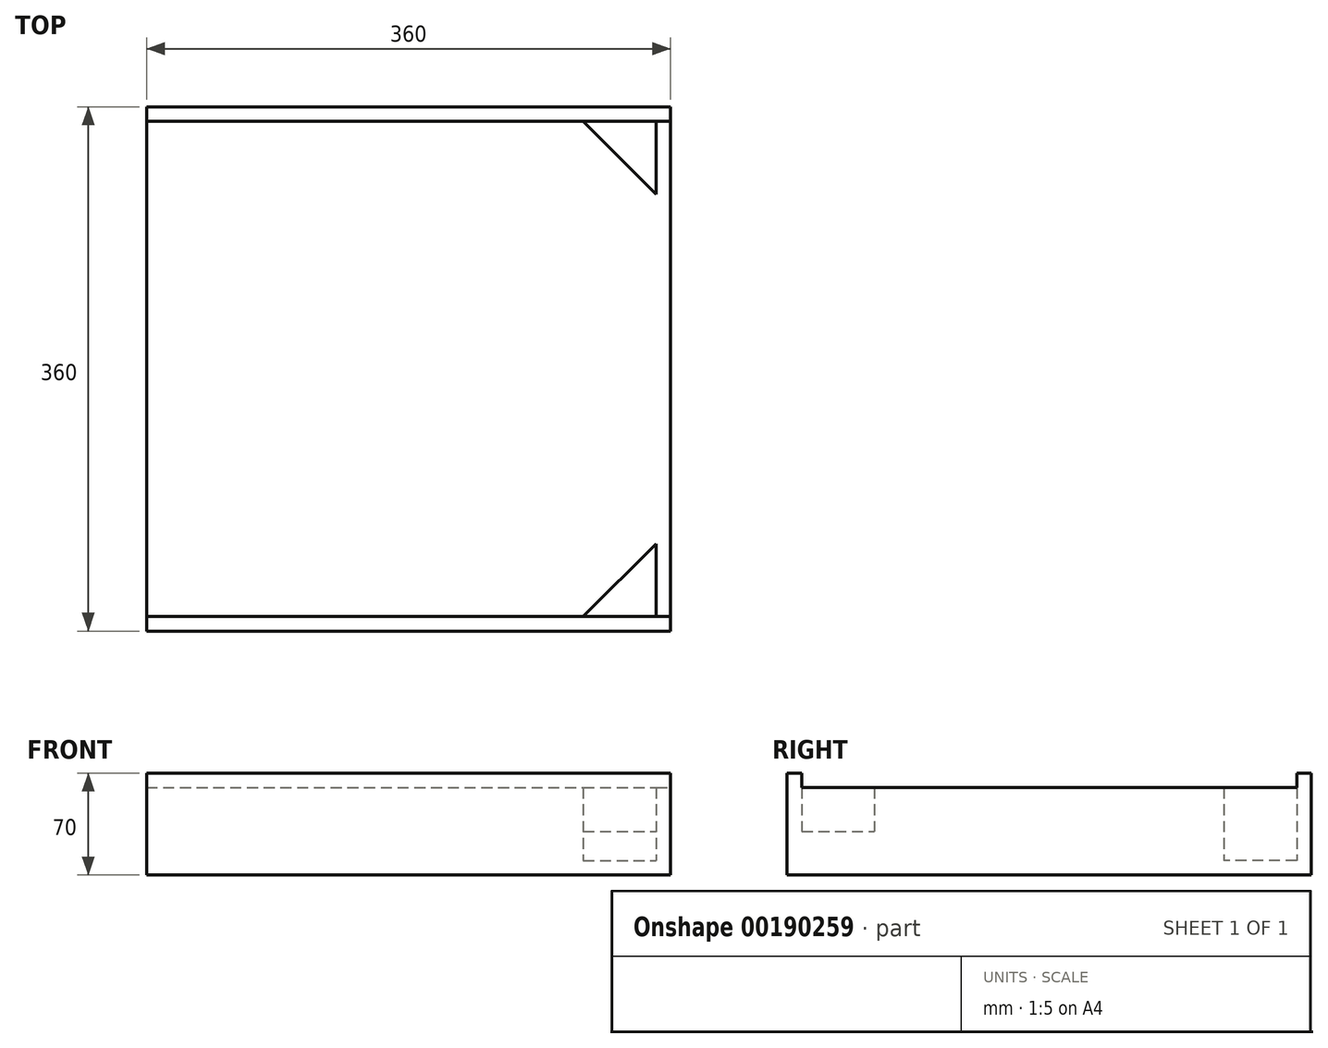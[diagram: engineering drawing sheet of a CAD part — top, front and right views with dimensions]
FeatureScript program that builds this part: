
annotation { "Feature Type Name" : "Feature", "Feature Type Description" : "" }
export const myFeature = defineFeature(function(context is Context, id is Id, definition is map)
    precondition{}
    {
        {
            assignVariable(context, id + "F0", {"name" : "Epb1", "anyValue" : 10});
        }
        {
            var Q0;
            Q0=qCreatedBy(makeId("Top.planeOp"),FACE);
            var sketch = newSketch(context, id + "F1", { "sketchPlane" : qUnion([Q0])});
            skCircle(sketch, "E0", {"center": v(0, 0) * mm, "radius": 150 * mm});
            skSolve(sketch);
        }
        {
            var Q0;
            Q0=makeQuery(id+"F1.imprint","IMPRINT",FACE,{"disambiguationData":[TD([[makeQuery(id+"F1.imprint","IMPRINT",EDGE,{"derivedFrom":sQuery(id+"F1.wireOp",EDGE,"E0")}),1.0]])]});
            extrude(context, id + "F2", {"entities" : qUnion([Q0]), "depth" : 35 * mm});
        }
        {
            var Q0;
            Q0=makeQuery(id+"F2.opExtrude","CAP_FACE",FACE,{"disambiguationData":[OSD([sQuery(id+"F1.wireOp",EDGE,"E0")])],"isStart":true});
            var sketch = newSketch(context, id + "F3", { "sketchPlane" : qUnion([Q0])});
            skLineSegment(sketch, "E1.bottom", {"start": v(-170, 170) * mm, "end": v(170, 170) * mm});
            skLineSegment(sketch, "E1.top", {"start": v(-170, -170) * mm, "end": v(170, -170) * mm});
            skLineSegment(sketch, "E1.left", {"start": v(-170, 170) * mm, "end": v(-170, -170) * mm});
            skLineSegment(sketch, "E1.right", {"start": v(170, 170) * mm, "end": v(170, -170) * mm});
            skPoint(sketch, "E1.middle", {"position": v(0, 0) * mm});
            skLineSegment(sketch, "E2", {"start": v(170, -170) * mm, "end": v(120, -170) * mm});
            skLineSegment(sketch, "E3", {"start": v(170, -170) * mm, "end": v(170, -120) * mm});
            skLineSegment(sketch, "E4", {"start": v(170, -120) * mm, "end": v(120, -170) * mm});
            skLineSegment(sketch, "E5.1.0", {"start": v(-170, -170) * mm, "end": v(-170, -120) * mm});
            skLineSegment(sketch, "E5.1.1", {"start": v(-170, -170) * mm, "end": v(-120, -170) * mm});
            skLineSegment(sketch, "E5.1.2", {"start": v(-120, -170) * mm, "end": v(-170, -120) * mm});
            skLineSegment(sketch, "E5.2.0", {"start": v(-170, 170) * mm, "end": v(-120, 170) * mm});
            skLineSegment(sketch, "E5.2.1", {"start": v(-170, 170) * mm, "end": v(-170, 120) * mm});
            skLineSegment(sketch, "E5.2.2", {"start": v(-170, 120) * mm, "end": v(-120, 170) * mm});
            skLineSegment(sketch, "E5.3.0", {"start": v(170, 170) * mm, "end": v(170, 120) * mm});
            skLineSegment(sketch, "E5.3.1", {"start": v(170, 170) * mm, "end": v(120, 170) * mm});
            skLineSegment(sketch, "E5.3.2", {"start": v(120, 170) * mm, "end": v(170, 120) * mm});
            skLineSegment(sketch, "E5.anchor1", {"start": v(0, 0) * mm, "end": v(120, -170) * mm, "construction": true});
            skLineSegment(sketch, "E5.anchor2", {"start": v(0, 0) * mm, "end": v(170, 120) * mm, "construction": true});
            skSolve(sketch);
        }
        {
            var Q0;
            Q0=makeQuery(id+"F3.imprint","IMPRINT",FACE,{"disambiguationData":[TD([[makeQuery(id+"F3.imprint","IMPRINT",EDGE,{"derivedFrom":sQuery(id+"F3.wireOp",EDGE,"E1.bottom")}),-1.0]])]});
            var Q1;
            Q1=makeQuery(id+"F3.imprint","IMPRINT",FACE,{"disambiguationData":[TD([[makeQuery(id+"F3.imprint","IMPRINT",EDGE,{"derivedFrom":makeQuery(id+"F2.opExtrude","CAP_EDGE",EDGE,{"disambiguationData":[OSD([sQuery(id+"F1.wireOp",EDGE,"E0")])],"isStart":true})}),-1.0]])]});
            extrude(context, id + "F4", {"entities" : qUnion([Q0, Q1]), "depth" : 10 * mm});
        }
        {
            var Q0;
            Q0=makeQuery(id+"F4.opExtrude","CAP_FACE",FACE,{"disambiguationData":[OSD([sQuery(id+"F3.wireOp",EDGE,"E1.bottom"),sQuery(id+"F3.wireOp",EDGE,"E1.top"),sQuery(id+"F3.wireOp",EDGE,"E1.left"),sQuery(id+"F3.wireOp",EDGE,"E1.right"),sQuery(id+"F3.wireOp",EDGE,"E4"),sQuery(id+"F3.wireOp",EDGE,"E5.1.2"),sQuery(id+"F3.wireOp",EDGE,"E5.2.2"),sQuery(id+"F3.wireOp",EDGE,"E5.3.2")])],"isStart":true});
            extrude(context, id + "F5", {"entities" : qUnion([Q0]), "depth" : 10 * mm});
        }
        {
            var Q0;
            Q0=makeQuery(id+"F4.opExtrude","CAP_FACE",FACE,{"disambiguationData":[OSD([sQuery(id+"F3.wireOp",EDGE,"E1.bottom"),sQuery(id+"F3.wireOp",EDGE,"E1.top"),sQuery(id+"F3.wireOp",EDGE,"E1.left"),sQuery(id+"F3.wireOp",EDGE,"E1.right"),sQuery(id+"F3.wireOp",EDGE,"E4"),sQuery(id+"F3.wireOp",EDGE,"E5.1.2"),sQuery(id+"F3.wireOp",EDGE,"E5.2.2"),sQuery(id+"F3.wireOp",EDGE,"E5.3.2")])],"isStart":false});
            var sketch = newSketch(context, id + "F6", { "sketchPlane" : qUnion([Q0])});
            skLineSegment(sketch, "E6.bottom", {"start": v(-180, 180) * mm, "end": v(180, 180) * mm});
            skLineSegment(sketch, "E6.top", {"start": v(-180, -180) * mm, "end": v(180, -180) * mm});
            skLineSegment(sketch, "E6.left", {"start": v(-180, 180) * mm, "end": v(-180, -180) * mm});
            skLineSegment(sketch, "E6.right", {"start": v(180, 180) * mm, "end": v(180, -180) * mm});
            skPoint(sketch, "E6.middle", {"position": v(0, 0) * mm});
            skSolve(sketch);
        }
        {
            var Q0;
            Q0=makeQuery(id+"F6.imprint","IMPRINT",FACE,{"disambiguationData":[TD([[makeQuery(id+"F6.imprint","IMPRINT",EDGE,{"derivedFrom":sQuery(id+"F6.wireOp",EDGE,"E6.bottom")}),-1.0]])]});
            var Q1;
            Q1=makeQuery(id+"F6.imprint","IMPRINT",FACE,{"disambiguationData":[TD([[makeQuery(id+"F6.imprint","IMPRINT",EDGE,{"derivedFrom":makeQuery(id+"F4.opExtrude","CAP_EDGE",EDGE,{"disambiguationData":[OSD([sQuery(id+"F3.wireOp",EDGE,"E1.bottom")])],"isStart":false})}),-1.0]])]});
            extrude(context, id + "F7", {"entities" : qUnion([Q0, Q1]), "depth" : (getVariable(context, 'Epb1')) * mm});
        }
        {
            var Q0;
            Q0=makeQuery(id+"F7.opExtrude","CAP_FACE",FACE,{"disambiguationData":[OSD([sQuery(id+"F6.wireOp",EDGE,"E6.bottom"),sQuery(id+"F6.wireOp",EDGE,"E6.top"),sQuery(id+"F6.wireOp",EDGE,"E6.left"),sQuery(id+"F6.wireOp",EDGE,"E6.right")])],"isStart":true});
            var sketch = newSketch(context, id + "F8", { "sketchPlane" : qUnion([Q0])});
            skLineSegment(sketch, "E7.bottom", {"start": v(-180, -180) * mm, "end": v(180, -180) * mm});
            skLineSegment(sketch, "E7.top", {"start": v(-180, -170) * mm, "end": v(180, -170) * mm});
            skLineSegment(sketch, "E7.left", {"start": v(-180, -180) * mm, "end": v(-180, -170) * mm});
            skLineSegment(sketch, "E7.right", {"start": v(180, -180) * mm, "end": v(180, -170) * mm});
            skLineSegment(sketch, "E8.bottom", {"start": v(-180, 180) * mm, "end": v(180, 180) * mm});
            skLineSegment(sketch, "E8.top", {"start": v(-180, 170) * mm, "end": v(180, 170) * mm});
            skLineSegment(sketch, "E8.left", {"start": v(-180, 180) * mm, "end": v(-180, 170) * mm});
            skLineSegment(sketch, "E8.right", {"start": v(180, 180) * mm, "end": v(180, 170) * mm});
            skLineSegment(sketch, "E9.bottom", {"start": v(-180, -170) * mm, "end": v(-170, -170) * mm});
            skLineSegment(sketch, "E9.top", {"start": v(-180, 170) * mm, "end": v(-170, 170) * mm});
            skLineSegment(sketch, "E9.left", {"start": v(-180, -170) * mm, "end": v(-180, 170) * mm});
            skLineSegment(sketch, "E9.right", {"start": v(-170, -170) * mm, "end": v(-170, 170) * mm});
            skLineSegment(sketch, "E10.bottom", {"start": v(180, -170) * mm, "end": v(170, -170) * mm});
            skLineSegment(sketch, "E10.top", {"start": v(180, 170) * mm, "end": v(170, 170) * mm});
            skLineSegment(sketch, "E10.left", {"start": v(180, -170) * mm, "end": v(180, 170) * mm});
            skLineSegment(sketch, "E10.right", {"start": v(170, -170) * mm, "end": v(170, 170) * mm});
            skSolve(sketch);
        }
        {
            var Q0;
            Q0=makeQuery(id+"F8.imprint","IMPRINT",FACE,{"disambiguationData":[TD([[makeQuery(id+"F8.imprint","IMPRINT",EDGE,{"derivedFrom":sQuery(id+"F8.wireOp",EDGE,"E7.bottom")}),1.0]])]});
            var Q1;
            Q1=makeQuery(id+"F8.imprint","IMPRINT",FACE,{"disambiguationData":[TD([[makeQuery(id+"F8.imprint","IMPRINT",EDGE,{"derivedFrom":sQuery(id+"F8.wireOp",EDGE,"E9.bottom")}),1.0]])]});
            var Q2;
            Q2=makeQuery(id+"F8.imprint","IMPRINT",FACE,{"disambiguationData":[TD([[makeQuery(id+"F8.imprint","IMPRINT",EDGE,{"derivedFrom":sQuery(id+"F8.wireOp",EDGE,"E8.bottom")}),-1.0]])]});
            var Q3;
            Q3=makeQuery(id+"F8.imprint","IMPRINT",FACE,{"disambiguationData":[TD([[makeQuery(id+"F8.imprint","IMPRINT",EDGE,{"derivedFrom":sQuery(id+"F8.wireOp",EDGE,"E10.bottom")}),-1.0]])]});
            extrude(context, id + "F9", {"entities" : qUnion([Q0, Q1, Q2, Q3]), "operationType" : NewBodyOperationType.ADD, "depth" : 60 * mm});
        }
        {
            var Q0;
            Q0=makeQuery(id+"F7.opExtrude","CAP_FACE",FACE,{"disambiguationData":[OSD([sQuery(id+"F6.wireOp",EDGE,"E6.bottom"),sQuery(id+"F6.wireOp",EDGE,"E6.top"),sQuery(id+"F6.wireOp",EDGE,"E6.left"),sQuery(id+"F6.wireOp",EDGE,"E6.right")])],"isStart":true});
            var sketch = newSketch(context, id + "F10", { "sketchPlane" : qUnion([Q0])});
            skLineSegment(sketch, "E11", {"start": v(170, -170) * mm, "end": v(120, -170) * mm});
            skLineSegment(sketch, "E12", {"start": v(170, -170) * mm, "end": v(170, -120) * mm});
            skLineSegment(sketch, "E13", {"start": v(170, -120) * mm, "end": v(120, -170) * mm});
            skLineSegment(sketch, "E14.1.0", {"start": v(170, 170) * mm, "end": v(170, 120) * mm});
            skLineSegment(sketch, "E14.1.1", {"start": v(120, 170) * mm, "end": v(170, 120) * mm});
            skLineSegment(sketch, "E14.1.2", {"start": v(170, 170) * mm, "end": v(120, 170) * mm});
            skLineSegment(sketch, "E14.2.0", {"start": v(-170, 170) * mm, "end": v(-120, 170) * mm});
            skLineSegment(sketch, "E14.2.1", {"start": v(-170, 120) * mm, "end": v(-120, 170) * mm});
            skLineSegment(sketch, "E14.2.2", {"start": v(-170, 170) * mm, "end": v(-170, 120) * mm});
            skLineSegment(sketch, "E14.3.0", {"start": v(-170, -170) * mm, "end": v(-170, -120) * mm});
            skLineSegment(sketch, "E14.3.1", {"start": v(-120, -170) * mm, "end": v(-170, -120) * mm});
            skLineSegment(sketch, "E14.3.2", {"start": v(-170, -170) * mm, "end": v(-120, -170) * mm});
            skPoint(sketch, "E14.center", {"position": v(0, 0) * mm});
            skSolve(sketch);
        }
        {
            var Q0;
            Q0=makeQuery(id+"F10.imprint","IMPRINT",FACE,{"disambiguationData":[TD([[makeQuery(id+"F10.imprint","IMPRINT",EDGE,{"derivedFrom":sQuery(id+"F10.wireOp",EDGE,"E14.3.0")}),-1.0]])]});
            var Q1;
            Q1=makeQuery(id+"F10.imprint","IMPRINT",FACE,{"disambiguationData":[TD([[makeQuery(id+"F10.imprint","IMPRINT",EDGE,{"derivedFrom":sQuery(id+"F10.wireOp",EDGE,"E11")}),1.0]])]});
            var Q2;
            Q2=makeQuery(id+"F10.imprint","IMPRINT",FACE,{"disambiguationData":[TD([[makeQuery(id+"F10.imprint","IMPRINT",EDGE,{"derivedFrom":sQuery(id+"F10.wireOp",EDGE,"E14.1.0")}),1.0]])]});
            var Q3;
            Q3=makeQuery(id+"F10.imprint","IMPRINT",FACE,{"disambiguationData":[TD([[makeQuery(id+"F10.imprint","IMPRINT",EDGE,{"derivedFrom":sQuery(id+"F10.wireOp",EDGE,"E14.2.0")}),-1.0]])]});
            extrude(context, id + "F11", {"entities" : qUnion([Q0, Q1, Q2, Q3]), "operationType" : NewBodyOperationType.ADD, "depth" : 50 * mm});
        }
    });
